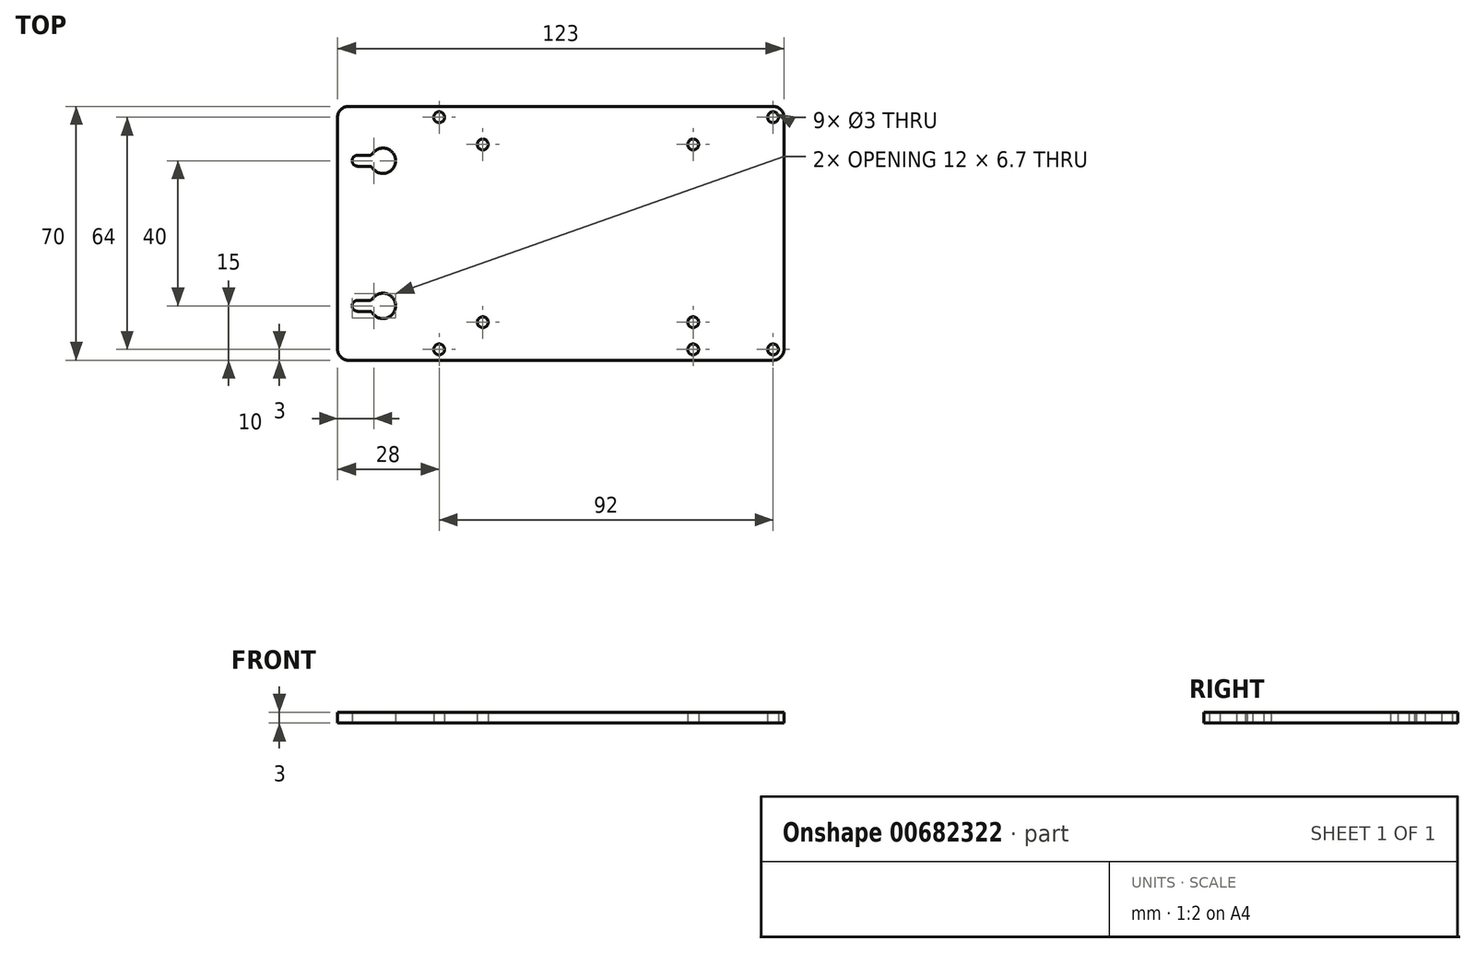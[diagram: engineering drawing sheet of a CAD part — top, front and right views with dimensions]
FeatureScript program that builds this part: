
annotation { "Feature Type Name" : "Feature", "Feature Type Description" : "" }
export const myFeature = defineFeature(function(context is Context, id is Id, definition is map)
    precondition{}
    {
        {
            var Q0;
            Q0=qCreatedBy(makeId("Top.planeOp"),FACE);
            var sketch = newSketch(context, id + "F0", { "sketchPlane" : qUnion([Q0])});
            skLineSegment(sketch, "E0.bottom", {"start": v(3, 0) * mm, "end": v(95, 0) * mm});
            skLineSegment(sketch, "E0.top", {"start": v(3, 70) * mm, "end": v(95, 70) * mm});
            skLineSegment(sketch, "E0.left", {"start": v(0, 3) * mm, "end": v(0, 67) * mm, "construction": true});
            skLineSegment(sketch, "E0.right", {"start": v(98, 3) * mm, "end": v(98, 67) * mm});
            skPoint(sketch, "E1.visualSharp", {"position": v(0, 70) * mm});
            skPoint(sketch, "E2.visualSharp", {"position": v(98, 70) * mm});
            skArc(sketch, "E2.filletArc", {"start": v(98, 67) * mm, "mid": v(97.12, 69.12) * mm, "end": v(95, 70) * mm});
            skPoint(sketch, "E3.visualSharp", {"position": v(98, 0) * mm});
            skArc(sketch, "E3.filletArc", {"start": v(95, 0) * mm, "mid": v(97.12, 0.88) * mm, "end": v(98, 3) * mm});
            skPoint(sketch, "E4.visualSharp", {"position": v(0, 0) * mm});
            skCircle(sketch, "E5", {"center": v(3, 67) * mm, "radius": 1.5 * mm});
            skCircle(sketch, "E6", {"center": v(95, 67) * mm, "radius": 1.5 * mm});
            skCircle(sketch, "E7", {"center": v(95, 3) * mm, "radius": 1.5 * mm});
            skCircle(sketch, "E8", {"center": v(3, 3) * mm, "radius": 1.5 * mm});
            skCircle(sketch, "E9", {"center": v(73, 3) * mm, "radius": 1.5 * mm});
            skLineSegment(sketch, "E10", {"start": v(0, 0) * mm, "end": v(-22, 0) * mm});
            skLineSegment(sketch, "E11", {"start": v(-25, 3) * mm, "end": v(-25, 67) * mm});
            skLineSegment(sketch, "E12", {"start": v(-22, 70) * mm, "end": v(0, 70) * mm});
            skLineSegment(sketch, "E13", {"start": v(3, 70) * mm, "end": v(0, 70) * mm});
            skLineSegment(sketch, "E14", {"start": v(3, 0) * mm, "end": v(0, 0) * mm});
            skPoint(sketch, "E15.visualSharp", {"position": v(-25, 70) * mm});
            skArc(sketch, "E15.filletArc", {"start": v(-22, 70) * mm, "mid": v(-24.12, 69.12) * mm, "end": v(-25, 67) * mm});
            skPoint(sketch, "E16.visualSharp", {"position": v(-25, 0) * mm});
            skArc(sketch, "E16.filletArc", {"start": v(-25, 3) * mm, "mid": v(-24.12, 0.88) * mm, "end": v(-22, 0) * mm});
            skLineSegment(sketch, "E17", {"start": v(15, 70) * mm, "end": v(15, 0) * mm, "construction": true});
            skLineSegment(sketch, "E18", {"start": v(-25, 59.5) * mm, "end": v(98, 59.5) * mm, "construction": true});
            skLineSegment(sketch, "E19", {"start": v(98, 10.5) * mm, "end": v(-25, 10.5) * mm, "construction": true});
            skLineSegment(sketch, "E20", {"start": v(73, 0) * mm, "end": v(73, 70) * mm, "construction": true});
            skCircle(sketch, "E21", {"center": v(15, 59.5) * mm, "radius": 1.5 * mm});
            skCircle(sketch, "E22", {"center": v(73, 59.5) * mm, "radius": 1.5 * mm});
            skCircle(sketch, "E23", {"center": v(73, 10.5) * mm, "radius": 1.5 * mm});
            skCircle(sketch, "E24", {"center": v(15, 10.5) * mm, "radius": 1.5 * mm});
            skPoint(sketch, "E25", {"position": v(15, 35) * mm});
            skLineSegment(sketch, "E26", {"start": v(-12.5, 70) * mm, "end": v(-12.5, 0) * mm, "construction": true});
            skArc(sketch, "E27", {"start": v(-15.41, 13.06) * mm, "mid": v(-9, 15) * mm, "end": v(-15.41, 16.94) * mm});
            skArc(sketch, "E28", {"start": v(-19.5, 16.5) * mm, "mid": v(-21, 15) * mm, "end": v(-19.5, 13.5) * mm});
            skLineSegment(sketch, "E29", {"start": v(-19.5, 16.5) * mm, "end": v(-16.24, 16.5) * mm});
            skLineSegment(sketch, "E30", {"start": v(-19.5, 13.5) * mm, "end": v(-16.24, 13.5) * mm});
            skLineSegment(sketch, "E31", {"start": v(-22.45, 35) * mm, "end": v(-2.82, 35) * mm, "construction": true});
            skPoint(sketch, "E32", {"position": v(-12.5, 35) * mm});
            skArc(sketch, "E33.MirrorCS", {"start": v(-15.41, 56.94) * mm, "mid": v(-9, 55) * mm, "end": v(-15.41, 53.06) * mm});
            skLineSegment(sketch, "E34.MirrorCS", {"start": v(-19.5, 53.5) * mm, "end": v(-16.24, 53.5) * mm});
            skArc(sketch, "E35.MirrorCS", {"start": v(-19.5, 53.5) * mm, "mid": v(-21, 55) * mm, "end": v(-19.5, 56.5) * mm});
            skLineSegment(sketch, "E36.MirrorCS", {"start": v(-19.5, 56.5) * mm, "end": v(-16.24, 56.5) * mm});
            skPoint(sketch, "E37.visualSharp", {"position": v(-15.66, 16.5) * mm});
            skArc(sketch, "E37.filletArc", {"start": v(-16.24, 16.5) * mm, "mid": v(-15.77, 16.62) * mm, "end": v(-15.41, 16.94) * mm});
            skPoint(sketch, "E38.visualSharp", {"position": v(-15.66, 13.5) * mm});
            skArc(sketch, "E38.filletArc", {"start": v(-15.41, 13.06) * mm, "mid": v(-15.77, 13.38) * mm, "end": v(-16.24, 13.5) * mm});
            skArc(sketch, "E39.MirrorCS", {"start": v(-16.24, 53.5) * mm, "mid": v(-15.77, 53.38) * mm, "end": v(-15.41, 53.06) * mm});
            skArc(sketch, "E40.MirrorCS", {"start": v(-15.41, 56.94) * mm, "mid": v(-15.77, 56.62) * mm, "end": v(-16.24, 56.5) * mm});
            skPoint(sketch, "E41.orphan", {"position": v(-15.66, 56.5) * mm});
            skPoint(sketch, "E42.orphan", {"position": v(-15.66, 53.5) * mm});
            skSolve(sketch);
        }
        {
            var Q0;
            Q0=makeQuery(id+"F0.imprint","IMPRINT",FACE,{"disambiguationData":[TD([[makeQuery(id+"F0.imprint","IMPRINT",EDGE,{"derivedFrom":sQuery(id+"F0.wireOp",EDGE,"E0.bottom")}),1.0]])]});
            extrude(context, id + "F1", {"entities" : qUnion([Q0]), "depth" : 3 * mm, "offsetDistance" : 25 * mm});
        }
    });
